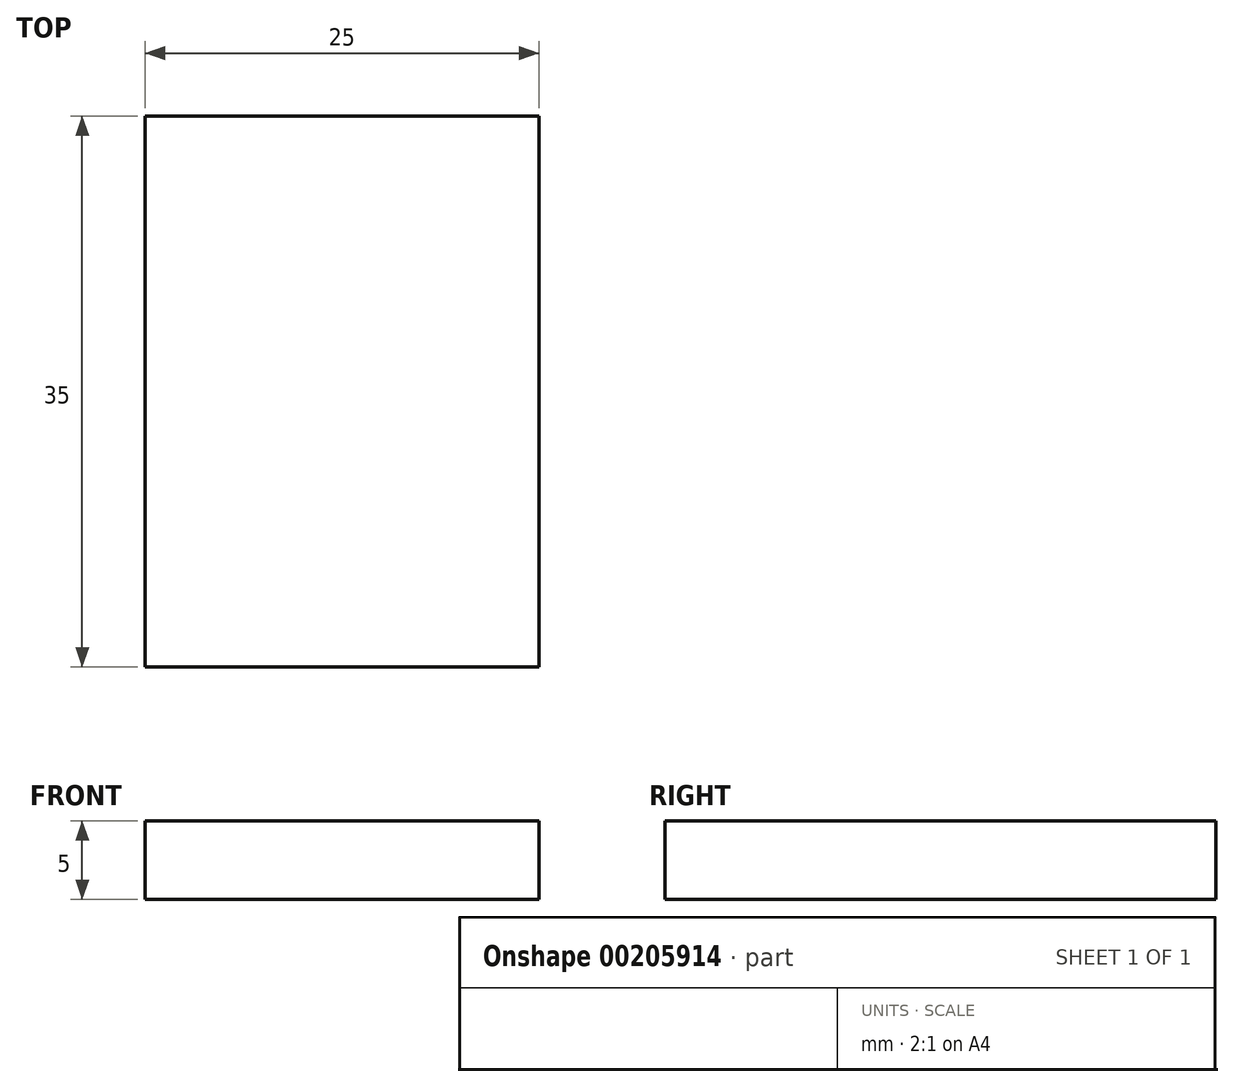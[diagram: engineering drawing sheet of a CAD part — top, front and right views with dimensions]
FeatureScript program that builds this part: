
annotation { "Feature Type Name" : "Feature", "Feature Type Description" : "" }
export const myFeature = defineFeature(function(context is Context, id is Id, definition is map)
    precondition{}
    {
        {
            var Q0;
            Q0=qCreatedBy(makeId("Front.planeOp"),FACE);
            var sketch = newSketch(context, id + "F0", { "sketchPlane" : qUnion([Q0])});
            skLineSegment(sketch, "E0.bottom", {"start": v(-43.96, 12.41) * mm, "end": v(-18.96, 12.41) * mm});
            skLineSegment(sketch, "E0.top", {"start": v(-43.96, 7.41) * mm, "end": v(-18.96, 7.41) * mm});
            skLineSegment(sketch, "E0.left", {"start": v(-43.96, 12.41) * mm, "end": v(-43.96, 7.41) * mm});
            skLineSegment(sketch, "E0.right", {"start": v(-18.96, 12.41) * mm, "end": v(-18.96, 7.41) * mm});
            skLineSegment(sketch, "E1.bottom", {"start": v(-28.96, 12.41) * mm, "end": v(-33.96, 12.41) * mm});
            skLineSegment(sketch, "E1.top", {"start": v(-28.96, 27.41) * mm, "end": v(-33.96, 27.41) * mm});
            skLineSegment(sketch, "E1.left", {"start": v(-28.96, 12.41) * mm, "end": v(-28.96, 27.41) * mm});
            skLineSegment(sketch, "E1.right", {"start": v(-33.96, 12.41) * mm, "end": v(-33.96, 27.41) * mm});
            skPoint(sketch, "E1.middle", {"position": v(-31.46, 19.91) * mm});
            skPoint(sketch, "E1.middle.positionSnap0", {"position": v(-31.46, 12.41) * mm});
            skPoint(sketch, "E1.centerSnap0", {"position": v(-31.46, 12.41) * mm});
            skSolve(sketch);
        }
        {
            var Q0;
            Q0=makeQuery(id+"F0.imprint","IMPRINT",FACE,{"disambiguationData":[TD([[makeQuery(id+"F0.imprint","IMPRINT",EDGE,{"derivedFrom":sQuery(id+"F0.wireOp",EDGE,"E1.bottom")}),-1.0]])]});
            var Q1;
            Q1=makeQuery(id+"F0.imprint","IMPRINT",FACE,{"disambiguationData":[TD([[makeQuery(id+"F0.imprint","IMPRINT",EDGE,{"derivedFrom":sQuery(id+"F0.wireOp",EDGE,"E0.top")}),1.0]])]});
            extrude(context, id + "F1", {"entities" : qUnion([Q0, Q1]), "depth" : 35 * mm});
        }
    });
